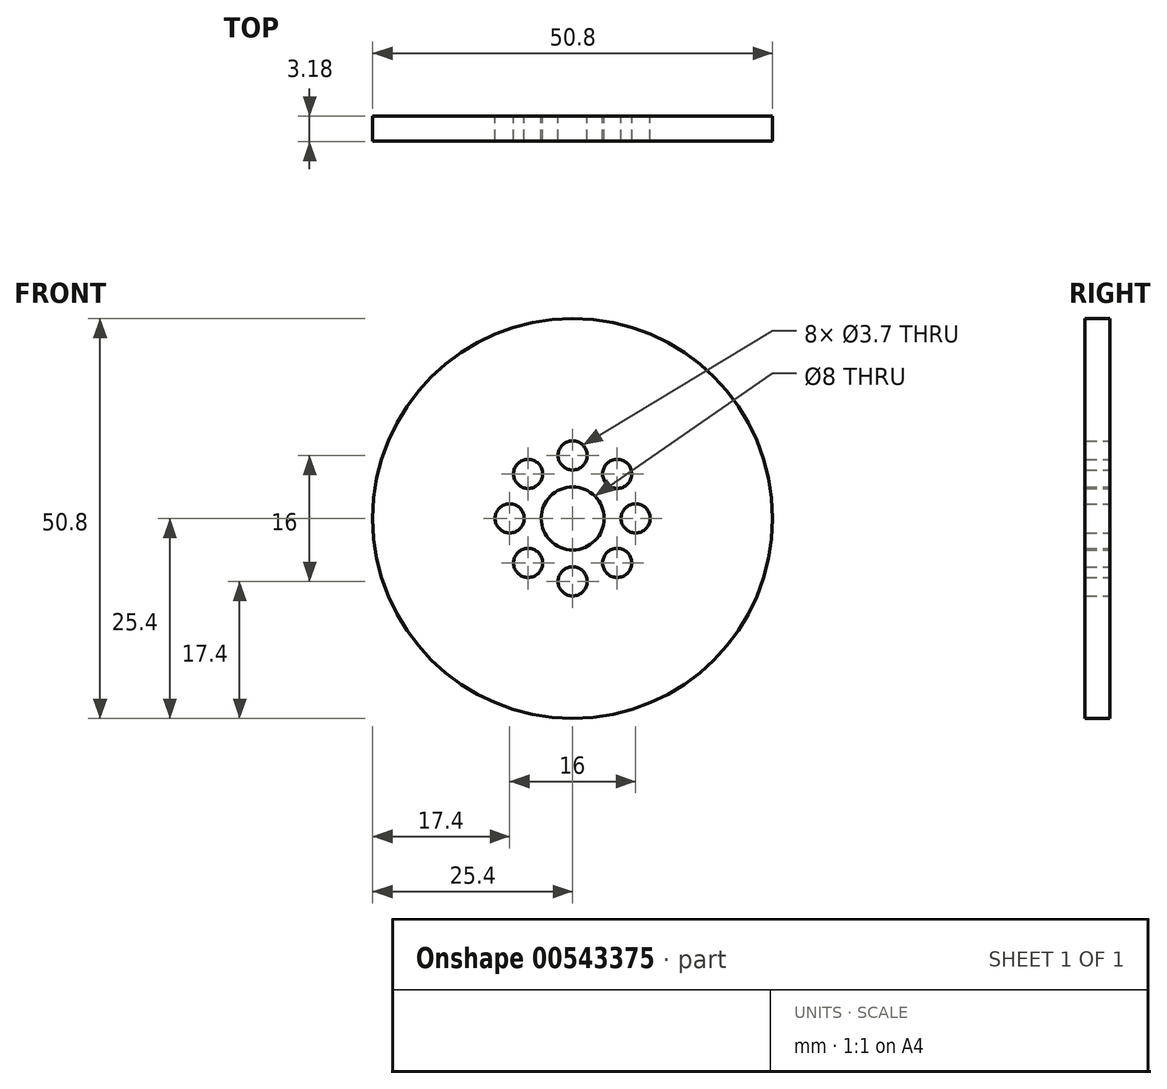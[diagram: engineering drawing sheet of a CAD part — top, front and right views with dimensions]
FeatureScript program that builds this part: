
annotation { "Feature Type Name" : "Feature", "Feature Type Description" : "" }
export const myFeature = defineFeature(function(context is Context, id is Id, definition is map)
    precondition{}
    {
        {
            var Q0;
            Q0=qCreatedBy(makeId("Front.planeOp"),FACE);
            var sketch = newSketch(context, id + "F0", { "sketchPlane" : qUnion([Q0])});
            skCircle(sketch, "E0", {"center": v(0, 0) * mm, "radius": 25.4 * mm});
            skCircle(sketch, "E1", {"center": v(0, 0) * mm, "radius": 4 * mm});
            skCircle(sketch, "E2", {"center": v(0, 8) * mm, "radius": 1.85 * mm});
            skCircle(sketch, "E3", {"center": v(0, -8) * mm, "radius": 1.85 * mm});
            skCircle(sketch, "E4", {"center": v(8, 0) * mm, "radius": 1.85 * mm});
            skCircle(sketch, "E5", {"center": v(-8, 0) * mm, "radius": 1.85 * mm});
            skCircle(sketch, "E6", {"center": v(0, 0) * mm, "radius": 8 * mm, "construction": true});
            skCircle(sketch, "E7", {"center": v(5.66, 5.66) * mm, "radius": 1.85 * mm});
            skCircle(sketch, "E8", {"center": v(-5.66, -5.66) * mm, "radius": 1.85 * mm});
            skLineSegment(sketch, "E9", {"start": v(-5.66, -5.66) * mm, "end": v(5.66, 5.66) * mm});
            skLineSegment(sketch, "E10", {"start": v(5.66, 5.66) * mm, "end": v(-5.66, -5.66) * mm});
            skLineSegment(sketch, "E11", {"start": v(-8, 0) * mm, "end": v(8, 0) * mm, "construction": true});
            skLineSegment(sketch, "E12", {"start": v(0, -8) * mm, "end": v(0, 8) * mm, "construction": true});
            skCircle(sketch, "E13", {"center": v(-5.66, 5.66) * mm, "radius": 1.85 * mm});
            skCircle(sketch, "E14", {"center": v(5.66, -5.66) * mm, "radius": 1.85 * mm});
            skLineSegment(sketch, "E15", {"start": v(-5.66, 5.66) * mm, "end": v(5.66, -5.66) * mm, "construction": true});
            skSolve(sketch);
        }
        {
            var Q0;
            Q0=makeQuery(id+"F0.imprint","IMPRINT",FACE,{"disambiguationData":[TD([[makeQuery(id+"F0.imprint","IMPRINT",EDGE,{"derivedFrom":sQuery(id+"F0.wireOp",EDGE,"E0")}),1.0]])]});
            extrude(context, id + "F1", {"entities" : qUnion([Q0]), "depth" : 3.17 * mm, "offsetDistance" : 25.4 * mm});
        }
    });
